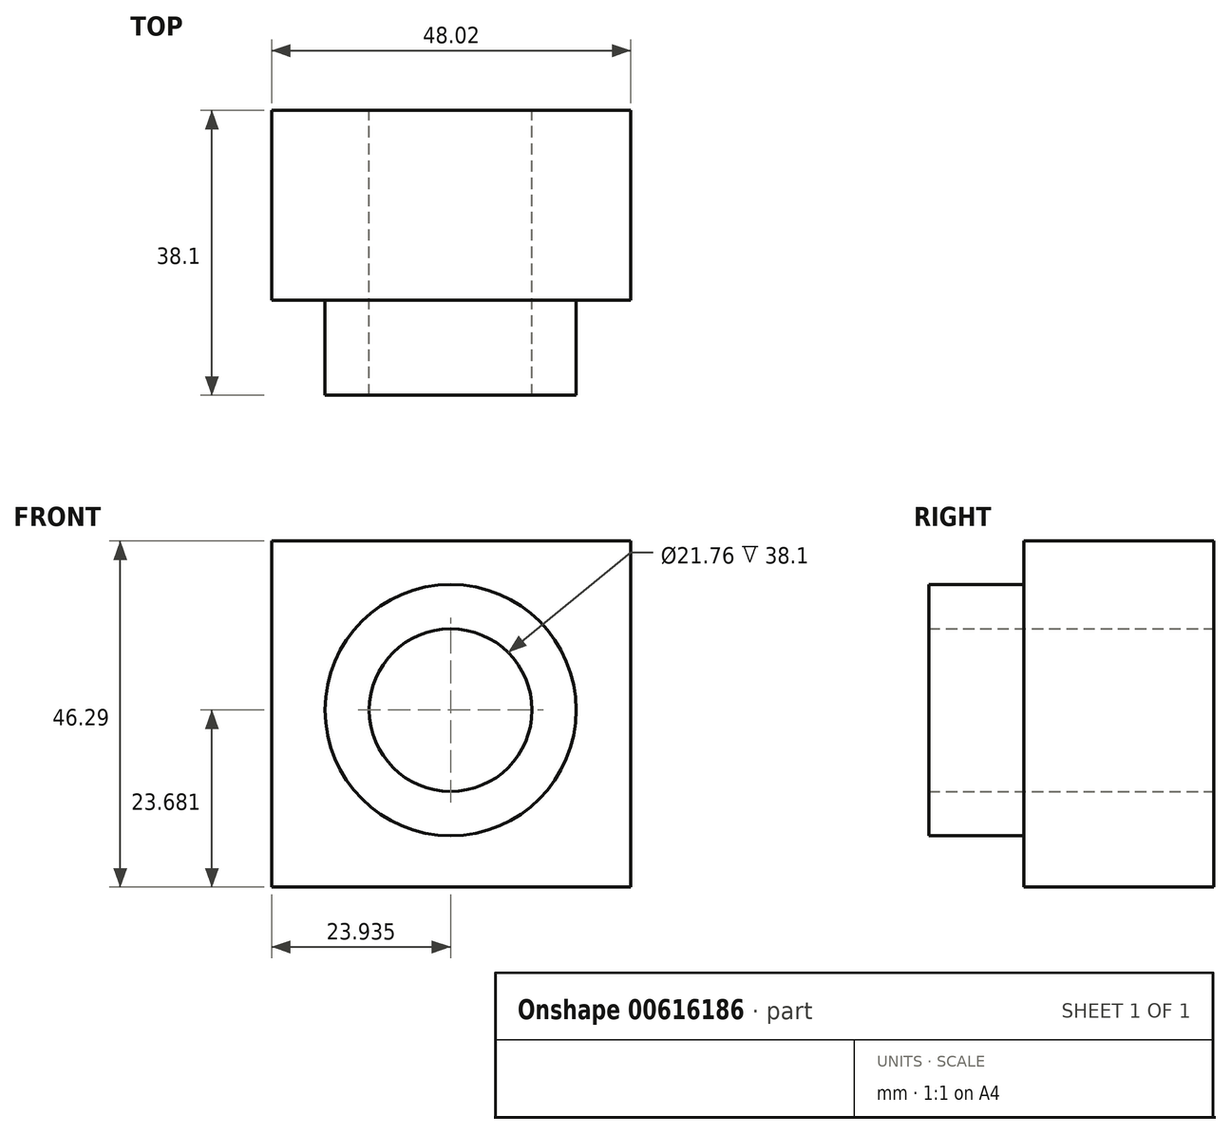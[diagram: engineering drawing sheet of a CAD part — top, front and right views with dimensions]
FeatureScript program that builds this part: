
annotation { "Feature Type Name" : "Feature", "Feature Type Description" : "" }
export const myFeature = defineFeature(function(context is Context, id is Id, definition is map)
    precondition{}
    {
        {
            var Q0;
            Q0=qCreatedBy(makeId("Front.planeOp"),FACE);
            var sketch = newSketch(context, id + "F0", { "sketchPlane" : qUnion([Q0])});
            skLineSegment(sketch, "E0.bottom", {"start": v(0, 0) * mm, "end": v(-52.77, 0) * mm});
            skLineSegment(sketch, "E0.top", {"start": v(0, 46.29) * mm, "end": v(-52.77, 46.29) * mm});
            skLineSegment(sketch, "E0.left", {"start": v(0, 0) * mm, "end": v(0, 46.29) * mm});
            skLineSegment(sketch, "E0.right", {"start": v(-52.77, 0) * mm, "end": v(-52.77, 46.29) * mm});
            skSolve(sketch);
        }
        {
            var Q0;
            Q0 = qSketchRegion(id + "F0", true);
            extrude(context, id + "F1", {"entities" : qUnion([Q0]), "depth" : 25.4 * mm, "offsetDistance" : 25.4 * mm});
        }
        {
            var Q0;
            Q0=makeQuery(id+"F1.opExtrude","CAP_FACE",FACE,{"disambiguationData":[OSD([sQuery(id+"F0.wireOp",EDGE,"E0.bottom"),sQuery(id+"F0.wireOp",EDGE,"E0.top"),sQuery(id+"F0.wireOp",EDGE,"E0.left"),sQuery(id+"F0.wireOp",EDGE,"E0.right")])],"isStart":false});
            var sketch = newSketch(context, id + "F2", { "sketchPlane" : qUnion([Q0])});
            skCircle(sketch, "E1", {"center": v(-28.84, 23.68) * mm, "radius": 16.8 * mm});
            skCircle(sketch, "E2", {"center": v(-28.84, 23.68) * mm, "radius": 10.88 * mm});
            skSolve(sketch);
        }
        {
            var Q0;
            Q0=makeQuery(id+"F2.imprint","IMPRINT",FACE,{"disambiguationData":[TD([[makeQuery(id+"F2.imprint","IMPRINT",EDGE,{"derivedFrom":sQuery(id+"F2.wireOp",EDGE,"E1")}),1.0]])]});
            extrude(context, id + "F3", {"entities" : qUnion([Q0]), "operationType" : NewBodyOperationType.ADD, "depth" : 12.7 * mm, "offsetDistance" : 25.4 * mm});
        }
        {
            var Q0;
            Q0=makeQuery(id+"F3.boolean.opBoolean","SPLIT",FACE,{"disambiguationData":[TD([makeQuery(id+"F3.opExtrude","SWEPT_FACE",FACE,{"disambiguationData":[OSD([sQuery(id+"F2.wireOp",EDGE,"E2")])]})])],"derivedFrom":makeQuery(id+"F1.opExtrude","CAP_FACE",FACE,{"disambiguationData":[OSD([sQuery(id+"F0.wireOp",EDGE,"E0.bottom"),sQuery(id+"F0.wireOp",EDGE,"E0.top"),sQuery(id+"F0.wireOp",EDGE,"E0.left"),sQuery(id+"F0.wireOp",EDGE,"E0.right")])],"isStart":false})});
            extrude(context, id + "F4", {"entities" : qUnion([Q0]), "operationType" : NewBodyOperationType.REMOVE, "oppositeDirection" : true, "depth" : 25.4 * mm, "offsetDistance" : 25.4 * mm});
        }
        {
            var Q0;
            {var subQ0=sQuery(id+"F0.wireOp",EDGE,"E0.left");var subQ1=sQuery(id+"F0.wireOp",EDGE,"E0.top");var subQ2=sQuery(id+"F0.wireOp",EDGE,"E0.right");var subQ3=sQuery(id+"F0.wireOp",EDGE,"E0.bottom");Q0=makeQuery(id+"F3.boolean.opBoolean","SPLIT",FACE,{"disambiguationData":[TD([makeQuery(id+"F1.opExtrude","SWEPT_FACE",FACE,{"disambiguationData":[OSD([subQ3])]})])],"derivedFrom":makeQuery(id+"F1.opExtrude","CAP_FACE",FACE,{"disambiguationData":[OSD([subQ3,subQ1,subQ0,subQ2])],"isStart":false})});}
            var sketch = newSketch(context, id + "F5", { "sketchPlane" : qUnion([Q0])});
            skLineSegment(sketch, "E3", {"start": v(-4.75, 46.29) * mm, "end": v(-4.75, 0) * mm});
            skLineSegment(sketch, "E4", {"start": v(-4.75, 0) * mm, "end": v(0, 0) * mm});
            skLineSegment(sketch, "E5", {"start": v(0, 0) * mm, "end": v(0, 46.29) * mm});
            skLineSegment(sketch, "E6", {"start": v(0, 46.29) * mm, "end": v(-4.75, 46.29) * mm});
            skSolve(sketch);
        }
        {
            var Q0;
            Q0=makeQuery(id+"F5.imprint","IMPRINT",FACE,{"disambiguationData":[TD([[makeQuery(id+"F5.imprint","IMPRINT",EDGE,{"derivedFrom":sQuery(id+"F5.wireOp",EDGE,"E3")}),1.0]])]});
            extrude(context, id + "F6", {"entities" : qUnion([Q0]), "operationType" : NewBodyOperationType.REMOVE, "oppositeDirection" : true, "depth" : 25.4 * mm, "offsetDistance" : 25.4 * mm});
        }
    });
